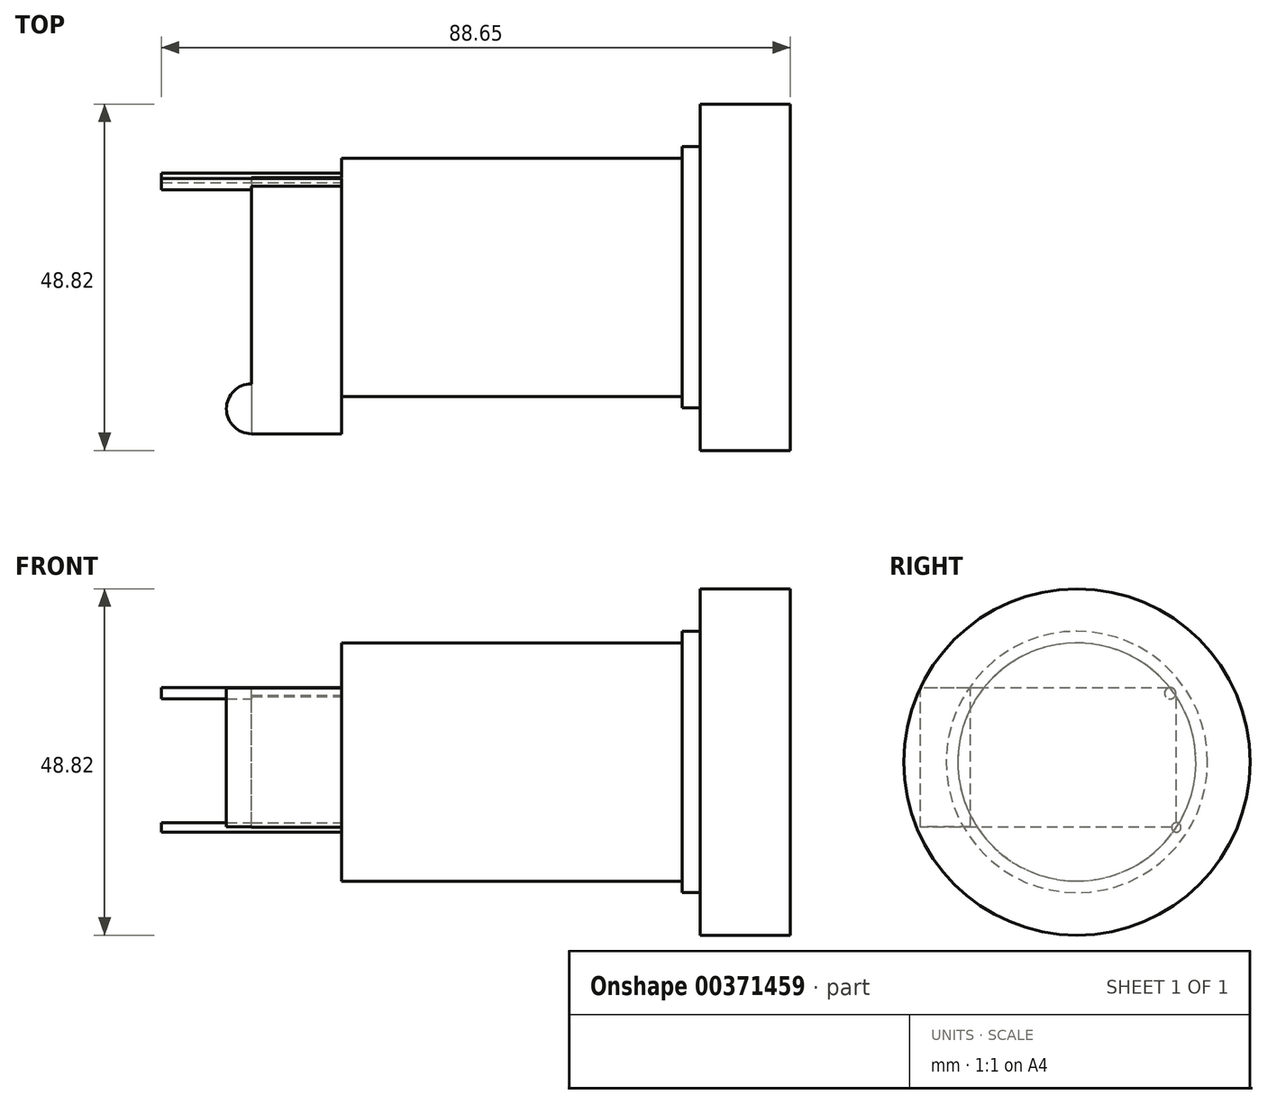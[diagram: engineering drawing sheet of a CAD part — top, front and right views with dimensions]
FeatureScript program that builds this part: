
annotation { "Feature Type Name" : "Feature", "Feature Type Description" : "" }
export const myFeature = defineFeature(function(context is Context, id is Id, definition is map)
    precondition{}
    {
        {
            var Q0;
            Q0=qCreatedBy(makeId("Right.planeOp"),FACE);
            var sketch = newSketch(context, id + "F0", { "sketchPlane" : qUnion([Q0])});
            skCircle(sketch, "E0", {"center": v(0, 0) * mm, "radius": 24.41 * mm});
            skSolve(sketch);
        }
        {
            var Q0;
            Q0 = qSketchRegion(id + "F0", true);
            extrude(context, id + "F1", {"entities" : qUnion([Q0]), "endBound" : BoundingType.SYMMETRIC, "depth" : 12.7 * mm});
        }
        {
            var Q0;
            Q0=makeQuery(id+"F1.opExtrude","CAP_FACE",FACE,{"disambiguationData":[OSD([sQuery(id+"F0.wireOp",EDGE,"E0")])],"isStart":true});
            var sketch = newSketch(context, id + "F2", { "sketchPlane" : qUnion([Q0])});
            skCircle(sketch, "E1", {"center": v(0, 0) * mm, "radius": 18.43 * mm});
            skSolve(sketch);
        }
        {
            var Q0;
            Q0 = qSketchRegion(id + "F2", true);
            extrude(context, id + "F3", {"entities" : qUnion([Q0]), "operationType" : NewBodyOperationType.ADD, "depth" : 2.54 * mm});
        }
        {
            var Q0;
            Q0=makeQuery(id+"F3.opExtrude","CAP_FACE",FACE,{"disambiguationData":[OSD([sQuery(id+"F2.wireOp",EDGE,"E1")])],"isStart":false});
            var sketch = newSketch(context, id + "F4", { "sketchPlane" : qUnion([Q0])});
            skCircle(sketch, "E2", {"center": v(0, 0) * mm, "radius": 11.35 * mm});
            skCircle(sketch, "E3", {"center": v(0, 0) * mm, "radius": 16.78 * mm});
            skSolve(sketch);
        }
        {
            var Q0;
            Q0=makeQuery(id+"F4.imprint","IMPRINT",FACE,{"disambiguationData":[TD([[makeQuery(id+"F4.imprint","IMPRINT",EDGE,{"derivedFrom":sQuery(id+"F4.wireOp",EDGE,"E2")}),1.0]])]});
            var Q1;
            Q1=makeQuery(id+"F4.imprint","IMPRINT",FACE,{"disambiguationData":[TD([[makeQuery(id+"F4.imprint","IMPRINT",EDGE,{"derivedFrom":sQuery(id+"F4.wireOp",EDGE,"E2")}),-1.0]])]});
            extrude(context, id + "F5", {"entities" : qUnion([Q0, Q1]), "operationType" : NewBodyOperationType.ADD, "depth" : 48 * mm});
        }
        {
            var Q0;
            Q0=makeQuery(id+"F5.opExtrude","CAP_FACE",FACE,{"disambiguationData":[OSD([sQuery(id+"F4.wireOp",EDGE,"E3")])],"isStart":false});
            var sketch = newSketch(context, id + "F6", { "sketchPlane" : qUnion([Q0])});
            skLineSegment(sketch, "E4.bottom", {"start": v(-14.02, -9.22) * mm, "end": v(22.06, -9.22) * mm});
            skLineSegment(sketch, "E4.top", {"start": v(-14.02, 10.42) * mm, "end": v(22.06, 10.42) * mm});
            skLineSegment(sketch, "E4.left", {"start": v(-14.02, -9.22) * mm, "end": v(-14.02, 10.42) * mm});
            skLineSegment(sketch, "E4.right", {"start": v(22.06, -9.22) * mm, "end": v(22.06, 10.42) * mm});
            skSolve(sketch);
        }
        {
            var Q0;
            {var subQ1=makeQuery(id+"F5.opExtrude","CAP_EDGE",EDGE,{"disambiguationData":[OSD([sQuery(id+"F4.wireOp",EDGE,"E3")])],"isStart":false});var subQ3=sQuery(id+"F6.wireOp",EDGE,"E4.top");var subQ7=makeQuery(id+"F6.imprint","INTERSECT",VERTEX,{"disambiguationData":[OD(0.0)],"derivedFrom":[subQ1,subQ3]});Q0=makeQuery(id+"F6.imprint","IMPRINT",FACE,{"disambiguationData":[TD([[makeQuery(id+"F6.imprint","IMPRINT",EDGE,{"disambiguationData":[TD([[subQ7,-1.0]])],"derivedFrom":subQ3}),-1.0]])]});}
            var Q1;
            {var subQ0=sQuery(id+"F6.wireOp",EDGE,"E4.right");Q1=makeQuery(id+"F6.imprint","IMPRINT",FACE,{"disambiguationData":[TD([[makeQuery(id+"F6.imprint","IMPRINT",EDGE,{"derivedFrom":subQ0}),1.0]])]});}
            extrude(context, id + "F7", {"entities" : qUnion([Q0, Q1]), "operationType" : NewBodyOperationType.ADD, "depth" : 12.7 * mm});
        }
        {
            var Q0;
            Q0=makeQuery(id+"F7.opExtrude","SWEPT_FACE",FACE,{"disambiguationData":[OSD([sQuery(id+"F6.wireOp",EDGE,"E4.bottom")])]});
            var sketch = newSketch(context, id + "F8", { "sketchPlane" : qUnion([Q0])});
            skSolve(sketch);
        }
        {
            var Q0;
            {var subQ0=sQuery(id+"F4.wireOp",EDGE,"E3");var subQ1=sQuery(id+"F6.wireOp",EDGE,"E4.top");Q0=makeQuery(id+"F7.boolean.opBoolean","SPLIT",FACE,{"disambiguationData":[TD([makeQuery(id+"F5.opExtrude","SWEPT_FACE",FACE,{"disambiguationData":[OSD([subQ0])]}),makeQuery(id+"F7.opExtrude","CAP_FACE",FACE,{"disambiguationData":[OSD([subQ0,sQuery(id+"F6.wireOp",EDGE,"E4.bottom"),subQ1,sQuery(id+"F6.wireOp",EDGE,"E4.left"),sQuery(id+"F6.wireOp",EDGE,"E4.right")])],"isStart":true}),makeQuery(id+"F7.opExtrude","SWEPT_FACE",FACE,{"disambiguationData":[OSD([subQ1])]}),makeQuery(id+"F7.opExtrude","SWEPT_FACE",FACE,{"disambiguationData":[OSD([subQ0])]})])],"derivedFrom":makeQuery(id+"F5.opExtrude","CAP_FACE",FACE,{"disambiguationData":[OSD([subQ0])],"isStart":false})});}
            var sketch = newSketch(context, id + "F9", { "sketchPlane" : qUnion([Q0])});
            skCircle(sketch, "E5", {"center": v(-13.16, 9.68) * mm, "radius": 0.8 * mm});
            skSolve(sketch);
        }
        {
            var Q0;
            Q0 = qSketchRegion(id + "F9", true);
            extrude(context, id + "F10", {"entities" : qUnion([Q0]), "operationType" : NewBodyOperationType.ADD, "depth" : 25.4 * mm});
        }
        {
            var Q0;
            {var subQ0=sQuery(id+"F6.wireOp",EDGE,"E4.bottom");var subQ1=sQuery(id+"F4.wireOp",EDGE,"E3");var subQ2=makeQuery(id+"F5.opExtrude","CAP_FACE",FACE,{"disambiguationData":[OSD([subQ1])],"isStart":false});var subQ3=sQuery(id+"F6.wireOp",EDGE,"E4.left");Q0=makeQuery(id+"F7.boolean.opBoolean","SPLIT",FACE,{"disambiguationData":[TD([makeQuery(id+"F5.opExtrude","SWEPT_FACE",FACE,{"disambiguationData":[OSD([subQ1])]}),subQ2,makeQuery(id+"F7.opExtrude","SWEPT_FACE",FACE,{"disambiguationData":[OSD([subQ0])]}),makeQuery(id+"F7.opExtrude","CAP_FACE",FACE,{"disambiguationData":[OSD([subQ1,subQ0,sQuery(id+"F6.wireOp",EDGE,"E4.top"),subQ3,sQuery(id+"F6.wireOp",EDGE,"E4.right")])],"isStart":true}),makeQuery(id+"F7.opExtrude","SWEPT_FACE",FACE,{"disambiguationData":[OSD([subQ3])]}),makeQuery(id+"F7.opExtrude","SWEPT_FACE",FACE,{"disambiguationData":[OSD([subQ1])]})])],"derivedFrom":subQ2});}
            var sketch = newSketch(context, id + "F11", { "sketchPlane" : qUnion([Q0])});
            skCircle(sketch, "E6", {"center": v(-14.02, -9.22) * mm, "radius": 0.66 * mm});
            skSolve(sketch);
        }
        {
            var Q0;
            Q0 = qSketchRegion(id + "F11", true);
            extrude(context, id + "F12", {"entities" : qUnion([Q0]), "operationType" : NewBodyOperationType.ADD, "depth" : 25.4 * mm});
        }
        {
            var Q0;
            Q0=makeQuery(id+"F7.opExtrude","SWEPT_FACE",FACE,{"disambiguationData":[OSD([sQuery(id+"F6.wireOp",EDGE,"E4.top")])]});
            var sketch = newSketch(context, id + "F13", { "sketchPlane" : qUnion([Q0])});
            skArc(sketch, "E7", {"start": v(-69.6, -15) * mm, "mid": v(-73.12, -18.53) * mm, "end": v(-69.6, -22.06) * mm});
            skArc(sketch, "E8", {"start": v(-92.68, -34.7) * mm, "mid": v(-95.44, -38.35) * mm, "end": v(-92.85, -42.12) * mm});
            skSolve(sketch);
        }
        {
            var Q0;
            Q0 = qSketchRegion(id + "F13", true);
            var Q1;
            {var subQ0=sQuery(id+"F13.wireOp",EDGE,"E7");Q1=makeQuery(id+"F13.imprint","IMPRINT",FACE,{"disambiguationData":[TD([[makeQuery(id+"F13.imprint","IMPRINT",EDGE,{"derivedFrom":subQ0}),1.0]])]});}
            extrude(context, id + "F14", {"entities" : qUnion([Q0, Q1]), "operationType" : NewBodyOperationType.ADD, "oppositeDirection" : true, "depth" : 2.54 * mm});
        }
        {
            var Q0;
            {var subQ0=sQuery(id+"F6.wireOp",EDGE,"E4.bottom");Q0=makeQuery(id+"F8.imprint","IMPRINT",FACE,{"disambiguationData":[TD([[makeQuery(id+"F8.imprint","IMPRINT",EDGE,{"derivedFrom":makeQuery(id+"F7.opExtrude","CAP_EDGE",EDGE,{"disambiguationData":[OSD([subQ0])],"isStart":false})}),-1.0]])]});}
            var sketch = newSketch(context, id + "F15", { "sketchPlane" : qUnion([Q0])});
            skArc(sketch, "E9", {"start": v(-69.58, 22.04) * mm, "mid": v(-73.07, 18.53) * mm, "end": v(-69.6, 14.99) * mm});
            skSolve(sketch);
        }
        {
            var Q0;
            Q0=makeQuery(id+"F14.opExtrude","CAP_FACE",FACE,{"disambiguationData":[OSD([sQuery(id+"F6.wireOp",EDGE,"E4.top"),sQuery(id+"F13.wireOp",EDGE,"E7")])],"isStart":false});
            var Q1;
            Q1=sQuery(id+"F15.wireOp",EDGE,"E9");
            extrude(context, id + "F16", {"entities" : qUnion([Q0]), "operationType" : NewBodyOperationType.ADD, "surfaceEntities" : qUnion([Q1]), "depth" : 17.02 * mm});
        }
    });
